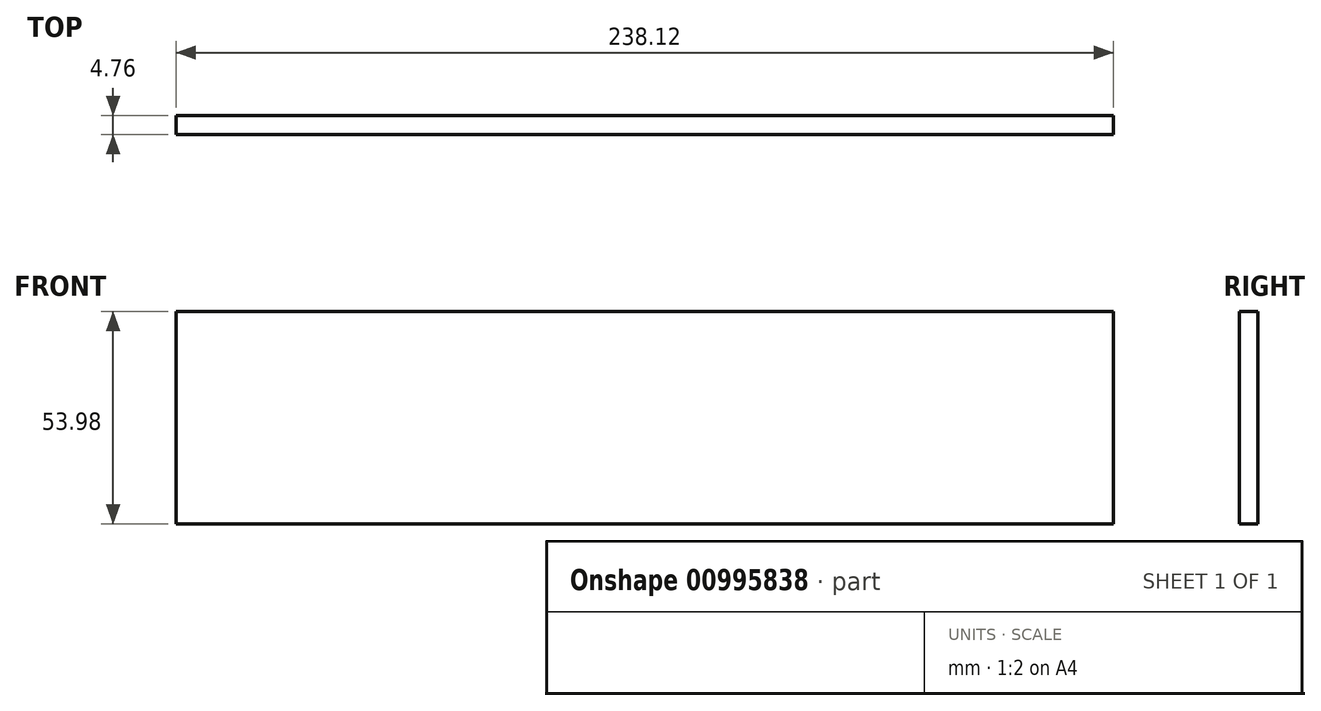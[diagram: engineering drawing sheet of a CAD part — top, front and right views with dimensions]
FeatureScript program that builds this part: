
annotation { "Feature Type Name" : "Feature", "Feature Type Description" : "" }
export const myFeature = defineFeature(function(context is Context, id is Id, definition is map)
    precondition{}
    {
        {
            var Q0;
            Q0=qCreatedBy(makeId("Front.planeOp"),FACE);
            var sketch = newSketch(context, id + "F0", { "sketchPlane" : qUnion([Q0])});
            skLineSegment(sketch, "E0.bottom", {"start": v(119.06, -26.99) * mm, "end": v(-119.06, -26.99) * mm});
            skLineSegment(sketch, "E0.top", {"start": v(119.06, 26.99) * mm, "end": v(-119.06, 26.99) * mm});
            skLineSegment(sketch, "E0.left", {"start": v(119.06, -26.99) * mm, "end": v(119.06, 26.99) * mm});
            skLineSegment(sketch, "E0.right", {"start": v(-119.06, -26.99) * mm, "end": v(-119.06, 26.99) * mm});
            skPoint(sketch, "E0.middle", {"position": v(0, 0) * mm});
            skSolve(sketch);
        }
        {
            var Q0;
            Q0 = qSketchRegion(id + "F0", true);
            extrude(context, id + "F1", {"entities" : qUnion([Q0]), "depth" : 4.76 * mm, "offsetDistance" : 25.4 * mm, "symmetric" : true});
        }
    });
